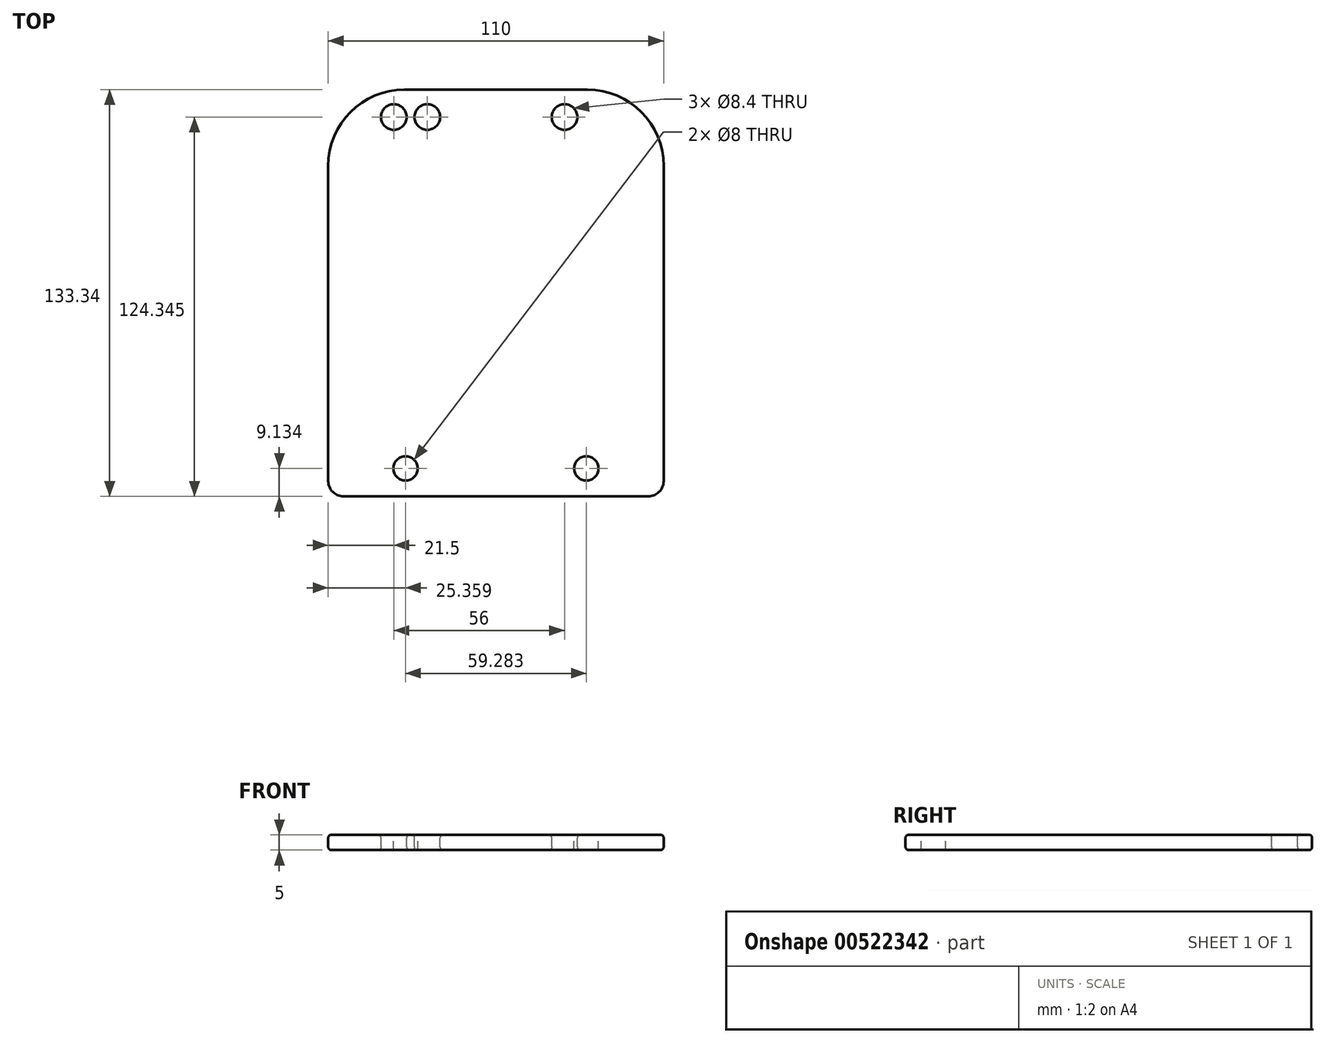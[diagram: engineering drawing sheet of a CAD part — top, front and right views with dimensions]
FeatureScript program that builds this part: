
annotation { "Feature Type Name" : "Feature", "Feature Type Description" : "" }
export const myFeature = defineFeature(function(context is Context, id is Id, definition is map)
    precondition{}
    {
        {
            var Q0;
            Q0=qCreatedBy(makeId("Top.planeOp"),FACE);
            var sketch = newSketch(context, id + "F0", { "sketchPlane" : qUnion([Q0])});
            skLineSegment(sketch, "E0.bottom", {"start": v(-30, 66.68) * mm, "end": v(30, 66.68) * mm});
            skLineSegment(sketch, "E0.top", {"start": v(-55, -66.67) * mm, "end": v(55, -66.67) * mm});
            skLineSegment(sketch, "E0.left", {"start": v(-55, 41.68) * mm, "end": v(-55, -66.67) * mm});
            skLineSegment(sketch, "E0.right", {"start": v(55, 41.68) * mm, "end": v(55, -66.67) * mm});
            skPoint(sketch, "E0.middle", {"position": v(0, 0) * mm});
            skCircle(sketch, "E1", {"center": v(22.5, 57.68) * mm, "radius": 25 * mm, "construction": true});
            skLineSegment(sketch, "E2", {"start": v(0, -2.6) * mm, "end": v(0, 84.85) * mm, "construction": true});
            skCircle(sketch, "E3.MirrorC", {"center": v(-22.5, 57.68) * mm, "radius": 25 * mm, "construction": true});
            skCircle(sketch, "E4", {"center": v(-22.5, 57.68) * mm, "radius": 4.2 * mm});
            skCircle(sketch, "E5.MirrorC", {"center": v(22.5, 57.68) * mm, "radius": 4.2 * mm});
            skPoint(sketch, "E6.visualSharp", {"position": v(-55, 66.68) * mm});
            skArc(sketch, "E6.filletArc", {"start": v(-30, 66.68) * mm, "mid": v(-47.68, 59.35) * mm, "end": v(-55, 41.68) * mm});
            skPoint(sketch, "E7.visualSharp", {"position": v(55, 66.68) * mm});
            skArc(sketch, "E7.filletArc", {"start": v(55, 41.68) * mm, "mid": v(47.68, 59.35) * mm, "end": v(30, 66.68) * mm});
            skLineSegment(sketch, "E8", {"start": v(22.5, 57.68) * mm, "end": v(-112.32, 57.67) * mm, "construction": true});
            skCircle(sketch, "E9", {"center": v(-33.5, 57.68) * mm, "radius": 4.2 * mm});
            skCircle(sketch, "E10", {"center": v(-33.5, 57.68) * mm, "radius": 25 * mm, "construction": true});
            skSolve(sketch);
        }
        {
            var Q0;
            Q0=qSketchRegion(id+"F0",true);
            extrude(context, id + "F1", {"entities" : qUnion([Q0]), "oppositeDirection" : true, "depth" : 5 * mm, "offsetDistance" : 25 * mm});
        }
        {
            var Q0;
            Q0=makeQuery(id+"F1.opExtrude","SWEPT_EDGE",EDGE,{"disambiguationData":[OSD([sQuery(id+"F0.wireOp",EDGE,"E0.top"),sQuery(id+"F0.wireOp",EDGE,"E0.right")])]});
            var Q1;
            Q1=makeQuery(id+"F1.opExtrude","SWEPT_EDGE",EDGE,{"disambiguationData":[OSD([sQuery(id+"F0.wireOp",EDGE,"E0.top"),sQuery(id+"F0.wireOp",EDGE,"E0.left")])]});
            fillet(context, id + "F2", {"entities" : qUnion([Q0, Q1]), "radius" : 5 * mm, "tangentPropagation" : true, "allowEdgeOverflow" : false});
        }
        {
            var Q0;
            Q0=makeQuery(id+"F1.opExtrude","CAP_FACE",FACE,{"disambiguationData":[OSD([sQuery(id+"F0.wireOp",EDGE,"E0.bottom"),sQuery(id+"F0.wireOp",EDGE,"E0.top"),sQuery(id+"F0.wireOp",EDGE,"E0.left"),sQuery(id+"F0.wireOp",EDGE,"E0.right"),sQuery(id+"F0.wireOp",EDGE,"E4"),sQuery(id+"F0.wireOp",EDGE,"E5.MirrorC"),sQuery(id+"F0.wireOp",EDGE,"E6.filletArc"),sQuery(id+"F0.wireOp",EDGE,"E7.filletArc")])],"isStart":true});
            var Q1;
            Q1=makeQuery(id+"F1.opExtrude","CAP_FACE",FACE,{"disambiguationData":[OSD([sQuery(id+"F0.wireOp",EDGE,"E0.bottom"),sQuery(id+"F0.wireOp",EDGE,"E0.top"),sQuery(id+"F0.wireOp",EDGE,"E0.left"),sQuery(id+"F0.wireOp",EDGE,"E0.right"),sQuery(id+"F0.wireOp",EDGE,"E4"),sQuery(id+"F0.wireOp",EDGE,"E5.MirrorC"),sQuery(id+"F0.wireOp",EDGE,"E6.filletArc"),sQuery(id+"F0.wireOp",EDGE,"E7.filletArc")])],"isStart":false});
            fillet(context, id + "F3", {"entities" : qUnion([Q0, Q1]), "radius" : 1 * mm, "tangentPropagation" : true, "allowEdgeOverflow" : false});
        }
        {
            var Q0;
            Q0=makeQuery(id+"F1.opExtrude","CAP_FACE",FACE,{"disambiguationData":[OSD([sQuery(id+"F0.wireOp",EDGE,"E0.bottom"),sQuery(id+"F0.wireOp",EDGE,"E0.top"),sQuery(id+"F0.wireOp",EDGE,"E0.left"),sQuery(id+"F0.wireOp",EDGE,"E0.right"),sQuery(id+"F0.wireOp",EDGE,"E4"),sQuery(id+"F0.wireOp",EDGE,"E5.MirrorC"),sQuery(id+"F0.wireOp",EDGE,"E6.filletArc"),sQuery(id+"F0.wireOp",EDGE,"E7.filletArc")])],"isStart":true});
            var sketch = newSketch(context, id + "F4", { "sketchPlane" : qUnion([Q0])});
            skCircle(sketch, "E11", {"center": v(29.64, -57.54) * mm, "radius": 4 * mm});
            skLineSegment(sketch, "E12", {"start": v(-1.39, 0) * mm, "end": v(-1.17, -1.75) * mm, "construction": true});
            skCircle(sketch, "E13.MirrorC", {"center": v(-29.64, -57.54) * mm, "radius": 4 * mm});
            skSolve(sketch);
        }
        {
            var Q0;
            Q0=qSketchRegion(id+"F4",true);
            extrude(context, id + "F5", {"entities" : qUnion([Q0]), "operationType" : NewBodyOperationType.REMOVE, "endBound" : BoundingType.THROUGH_ALL, "oppositeDirection" : true, "depth" : 25 * mm});
        }
    });
